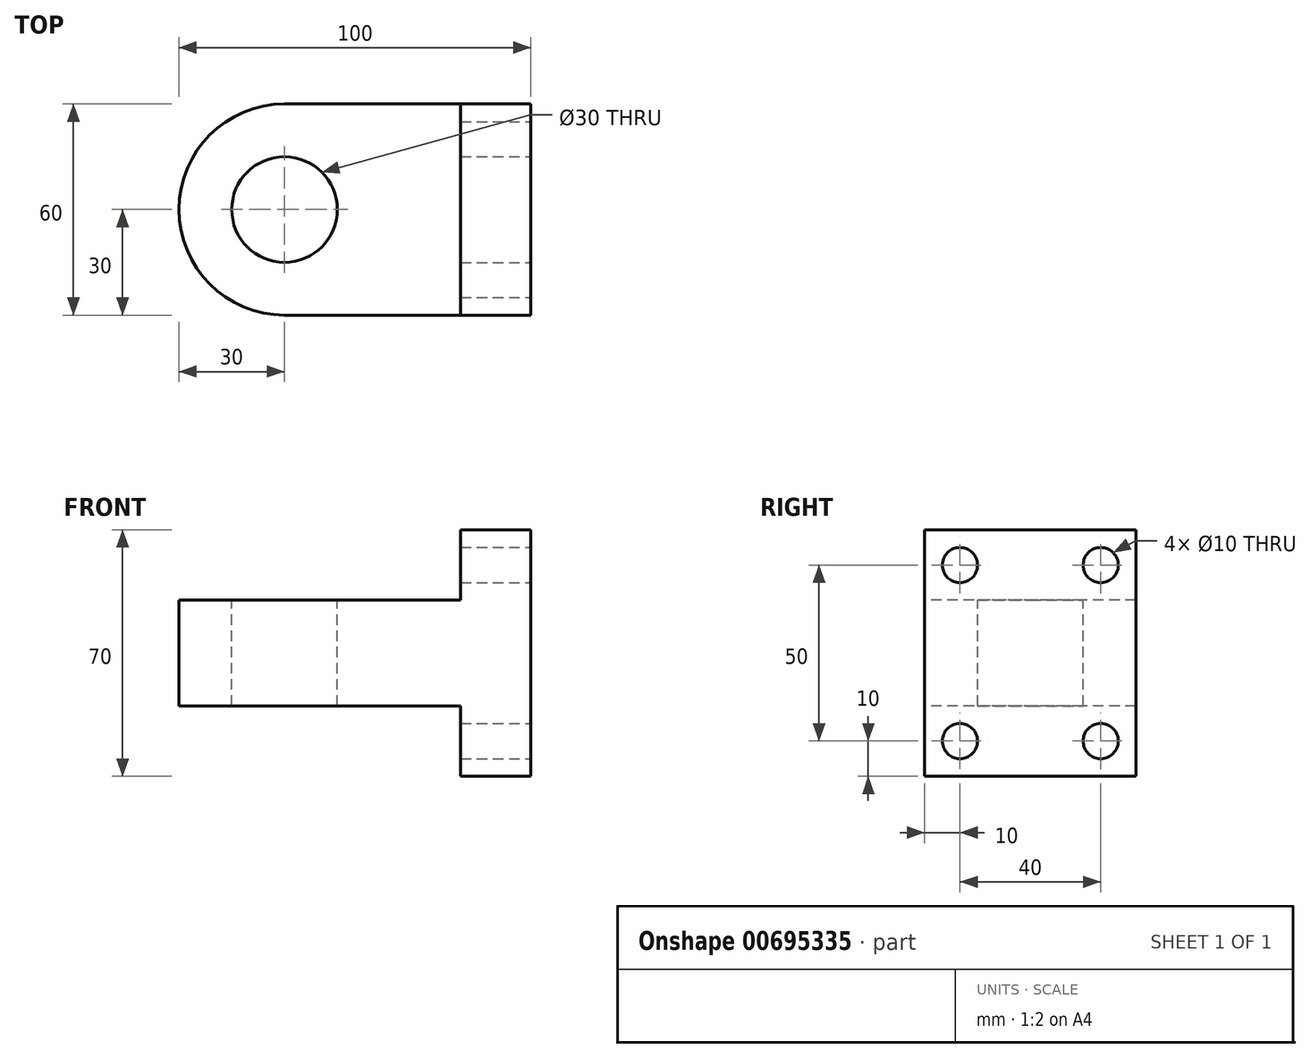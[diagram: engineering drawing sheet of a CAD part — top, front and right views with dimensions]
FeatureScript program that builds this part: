
annotation { "Feature Type Name" : "Feature", "Feature Type Description" : "" }
export const myFeature = defineFeature(function(context is Context, id is Id, definition is map)
    precondition{}
    {
        {
            var Q0;
            Q0=qCreatedBy(makeId("Front.planeOp"),FACE);
            var sketch = newSketch(context, id + "F0", { "sketchPlane" : qUnion([Q0])});
            skLineSegment(sketch, "E0", {"start": v(0, 0) * mm, "end": v(0, 35) * mm});
            skLineSegment(sketch, "E1", {"start": v(0, 35) * mm, "end": v(-20, 35) * mm});
            skLineSegment(sketch, "E2", {"start": v(-20, 35) * mm, "end": v(-20, 15) * mm});
            skLineSegment(sketch, "E3", {"start": v(-20, 15) * mm, "end": v(-100, 15) * mm});
            skLineSegment(sketch, "E4", {"start": v(-100, 15) * mm, "end": v(-100, 0) * mm});
            skLineSegment(sketch, "E5", {"start": v(-100, 0) * mm, "end": v(0, 0) * mm});
            skSolve(sketch);
        }
        {
            var Q0;
            Q0 = qSketchRegion(id + "F0", true);
            extrude(context, id + "F1", {"entities" : qUnion([Q0]), "endBound" : BoundingType.SYMMETRIC, "oppositeDirection" : true, "depth" : 60 * mm, "offsetDistance" : 25 * mm});
        }
        {
            var Q0;
            Q0=makeQuery(id+"F1.opExtrude","CAP_EDGE",EDGE,{"disambiguationData":[OSD([sQuery(id+"F0.wireOp",EDGE,"E4")])],"isStart":true});
            var Q1;
            Q1=makeQuery(id+"F1.opExtrude","CAP_EDGE",EDGE,{"disambiguationData":[OSD([sQuery(id+"F0.wireOp",EDGE,"E4")])],"isStart":false});
            fillet(context, id + "F2", {"entities" : qUnion([Q0, Q1]), "radius" : 30 * mm, "tangentPropagation" : true, "allowEdgeOverflow" : false});
        }
        {
            var Q0;
            Q0=makeQuery(id+"F1.opExtrude","SWEPT_FACE",FACE,{"disambiguationData":[OSD([sQuery(id+"F0.wireOp",EDGE,"E3")])]});
            var sketch = newSketch(context, id + "F3", { "sketchPlane" : qUnion([Q0])});
            skCircle(sketch, "E6", {"center": v(-70, 0) * mm, "radius": 15 * mm});
            skSolve(sketch);
        }
        {
            var Q0;
            Q0=makeQuery(id+"F3.imprint","IMPRINT",FACE,{"disambiguationData":[TD([[makeQuery(id+"F3.imprint","IMPRINT",EDGE,{"derivedFrom":sQuery(id+"F3.wireOp",EDGE,"E6")}),1.0]])]});
            extrude(context, id + "F4", {"entities" : qUnion([Q0]), "operationType" : NewBodyOperationType.REMOVE, "endBound" : BoundingType.UP_TO_NEXT, "oppositeDirection" : true, "depth" : 25 * mm, "offsetDistance" : 25 * mm});
        }
        {
            var Q0;
            Q0=makeQuery(id+"F1.opExtrude","SWEPT_BODY",BODY,{"disambiguationData":[OSD([sQuery(id+"F0.wireOp",EDGE,"E0"),sQuery(id+"F0.wireOp",EDGE,"E1"),sQuery(id+"F0.wireOp",EDGE,"E2"),sQuery(id+"F0.wireOp",EDGE,"E3"),sQuery(id+"F0.wireOp",EDGE,"E4"),sQuery(id+"F0.wireOp",EDGE,"E5")])]});
            var Q1;
            Q1=qCreatedBy(makeId("Top.planeOp"),FACE);
            mirror(context, id + "F5", {"operationType" : NewBodyOperationType.ADD, "entities" : qUnion([Q0]), "mirrorPlane" : qUnion([Q1])});
        }
        {
            var Q0;
            {var subQ0=makeQuery(id+"F1.opExtrude","SWEPT_FACE",FACE,{"disambiguationData":[OSD([sQuery(id+"F0.wireOp",EDGE,"E0")])]});Q0=makeQuery(id+"F5.boolean.opBoolean","MERGE",FACE,{"derivedFrom":[subQ0,makeQuery(id+"F5.opPattern","COPY",FACE,{"derivedFrom":subQ0,"instanceName":"1"})]});}
            var sketch = newSketch(context, id + "F6", { "sketchPlane" : qUnion([Q0])});
            skLineSegment(sketch, "E7", {"start": v(-30, -35) * mm, "end": v(-20, -35) * mm});
            skLineSegment(sketch, "E8", {"start": v(-20, -35) * mm, "end": v(-20, -25) * mm});
            skCircle(sketch, "E9", {"center": v(-20, -25) * mm, "radius": 5 * mm});
            skCircle(sketch, "E10.0.1.0", {"center": v(-20, 25) * mm, "radius": 5 * mm});
            skCircle(sketch, "E10.1.0.0", {"center": v(20, -25) * mm, "radius": 5 * mm});
            skCircle(sketch, "E10.1.1.0", {"center": v(20, 25) * mm, "radius": 5 * mm});
            skLineSegment(sketch, "E10.direction1", {"start": v(-20, -25) * mm, "end": v(20, -25) * mm, "construction": true});
            skLineSegment(sketch, "E10.direction2", {"start": v(-20, -25) * mm, "end": v(-20, 25) * mm, "construction": true});
            skSolve(sketch);
        }
        {
            var Q0;
            Q0 = qSketchRegion(id + "F6", true);
            extrude(context, id + "F7", {"entities" : qUnion([Q0]), "operationType" : NewBodyOperationType.REMOVE, "endBound" : BoundingType.UP_TO_NEXT, "oppositeDirection" : true, "depth" : 25 * mm, "offsetDistance" : 25 * mm});
        }
    });
